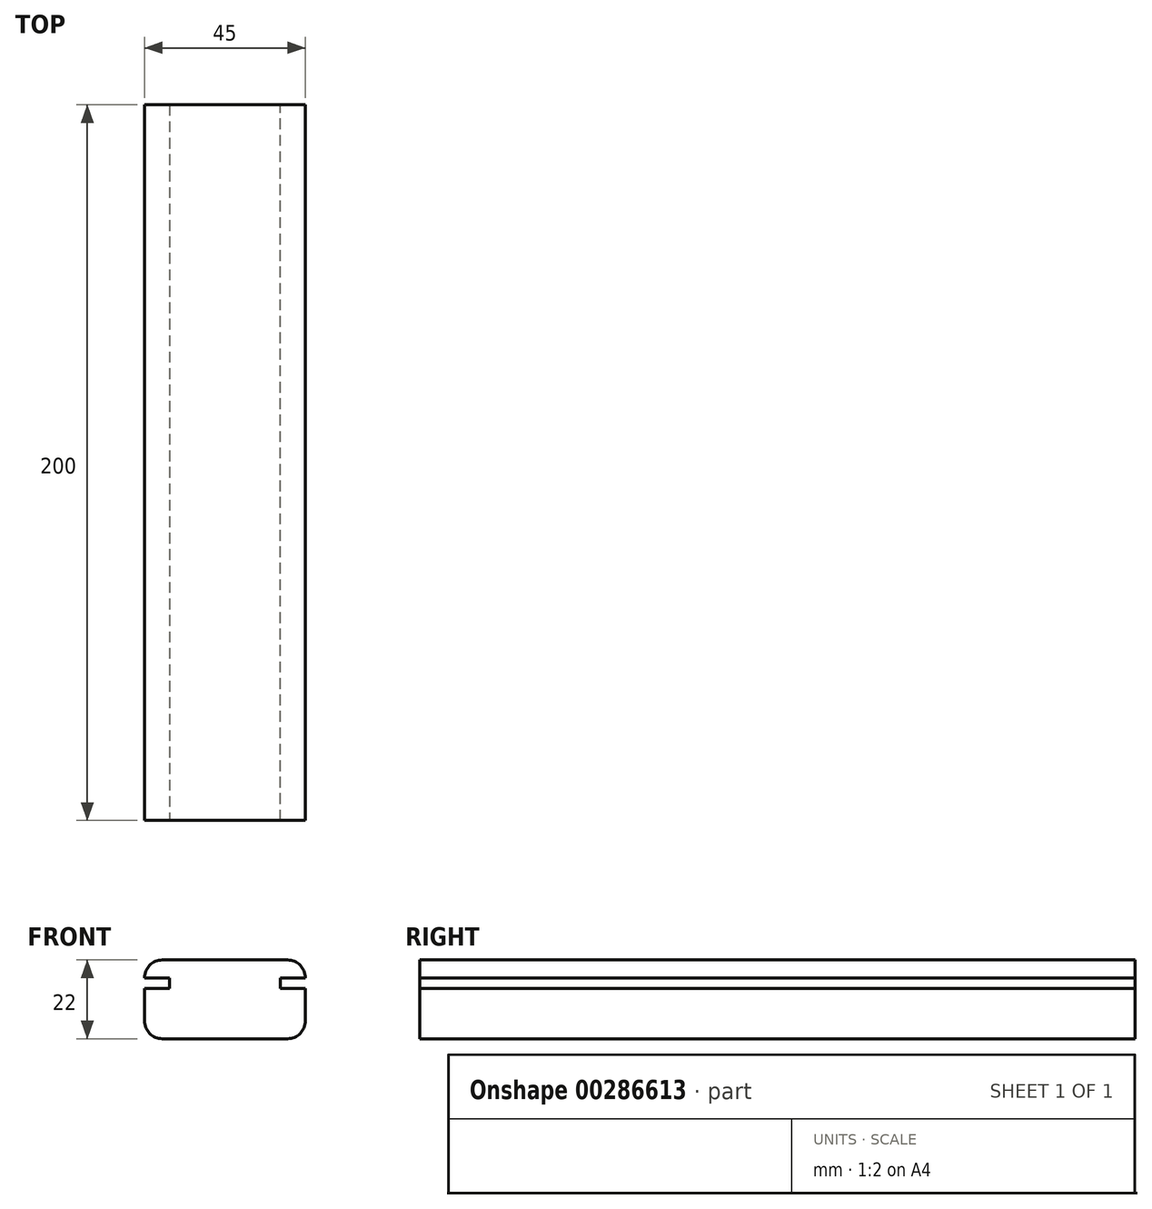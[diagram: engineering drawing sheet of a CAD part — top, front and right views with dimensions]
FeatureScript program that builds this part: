
annotation { "Feature Type Name" : "Feature", "Feature Type Description" : "" }
export const myFeature = defineFeature(function(context is Context, id is Id, definition is map)
    precondition{}
    {
        {
            var Q0;
            Q0=qCreatedBy(makeId("Front.planeOp"),FACE);
            var sketch = newSketch(context, id + "F0", { "sketchPlane" : qUnion([Q0])});
            skLineSegment(sketch, "E0.bottom", {"start": v(-22.5, 11) * mm, "end": v(22.5, 11) * mm});
            skLineSegment(sketch, "E0.top", {"start": v(-22.5, -11) * mm, "end": v(22.5, -11) * mm});
            skLineSegment(sketch, "E0.left", {"start": v(-22.5, 11) * mm, "end": v(-22.5, -11) * mm});
            skLineSegment(sketch, "E0.right", {"start": v(22.5, 11) * mm, "end": v(22.5, -11) * mm});
            skPoint(sketch, "E0.middle", {"position": v(0, 0) * mm});
            skSolve(sketch);
        }
        {
            var Q0;
            Q0=makeQuery(id+"F0.imprint","IMPRINT",FACE,{"disambiguationData":[TD([[makeQuery(id+"F0.imprint","IMPRINT",EDGE,{"derivedFrom":sQuery(id+"F0.wireOp",EDGE,"E0.bottom")}),-1.0]])]});
            extrude(context, id + "F1", {"entities" : qUnion([Q0]), "oppositeDirection" : true, "depth" : 200 * mm});
        }
        {
            var Q0;
            Q0=makeQuery(id+"F1.opExtrude","SWEPT_EDGE",EDGE,{"disambiguationData":[OSD([sQuery(id+"F0.wireOp",EDGE,"E0.bottom"),sQuery(id+"F0.wireOp",EDGE,"E0.right")])]});
            var Q1;
            Q1=makeQuery(id+"F1.opExtrude","SWEPT_EDGE",EDGE,{"disambiguationData":[OSD([sQuery(id+"F0.wireOp",EDGE,"E0.bottom"),sQuery(id+"F0.wireOp",EDGE,"E0.left")])]});
            var Q2;
            Q2=makeQuery(id+"F1.opExtrude","SWEPT_EDGE",EDGE,{"disambiguationData":[OSD([sQuery(id+"F0.wireOp",EDGE,"E0.top"),sQuery(id+"F0.wireOp",EDGE,"E0.right")])]});
            var Q3;
            Q3=makeQuery(id+"F1.opExtrude","SWEPT_EDGE",EDGE,{"disambiguationData":[OSD([sQuery(id+"F0.wireOp",EDGE,"E0.top"),sQuery(id+"F0.wireOp",EDGE,"E0.left")])]});
            fillet(context, id + "F2", {"entities" : qUnion([Q0, Q1, Q2, Q3]), "radius" : 5 * mm, "tangentPropagation" : true, "allowEdgeOverflow" : false});
        }
        {
            var Q0;
            Q0=makeQuery(id+"F1.opExtrude","SWEPT_FACE",FACE,{"disambiguationData":[OSD([sQuery(id+"F0.wireOp",EDGE,"E0.right")])]});
            var sketch = newSketch(context, id + "F3", { "sketchPlane" : qUnion([Q0])});
            skLineSegment(sketch, "E1.bottom", {"start": v(0, 3) * mm, "end": v(200, 3) * mm});
            skLineSegment(sketch, "E1.top", {"start": v(0, 6) * mm, "end": v(200, 6) * mm});
            skLineSegment(sketch, "E1.left", {"start": v(0, 3) * mm, "end": v(0, 6) * mm});
            skLineSegment(sketch, "E1.right", {"start": v(200, 3) * mm, "end": v(200, 6) * mm});
            skSolve(sketch);
        }
        {
            var Q0;
            {var subQ0=sQuery(id+"F3.wireOp",EDGE,"E1.top");Q0=makeQuery(id+"F3.imprint","IMPRINT",FACE,{"disambiguationData":[TD([[makeQuery(id+"F3.imprint","IMPRINT",EDGE,{"derivedFrom":subQ0}),-1.0]])]});}
            var Q1;
            {var subQ0=sQuery(id+"F3.wireOp",EDGE,"E1.bottom");Q1=makeQuery(id+"F3.imprint","IMPRINT",FACE,{"disambiguationData":[TD([[makeQuery(id+"F3.imprint","IMPRINT",EDGE,{"derivedFrom":subQ0}),1.0]])]});}
            extrude(context, id + "F4", {"entities" : qUnion([Q0, Q1]), "operationType" : NewBodyOperationType.REMOVE, "oppositeDirection" : true, "depth" : 7 * mm});
        }
        {
            var Q0;
            Q0=makeQuery(id+"F1.opExtrude","SWEPT_FACE",FACE,{"disambiguationData":[OSD([sQuery(id+"F0.wireOp",EDGE,"E0.left")])]});
            var sketch = newSketch(context, id + "F5", { "sketchPlane" : qUnion([Q0])});
            skLineSegment(sketch, "E2.bottom", {"start": v(-200, 3) * mm, "end": v(0, 3) * mm});
            skLineSegment(sketch, "E2.top", {"start": v(-200, 6) * mm, "end": v(0, 6) * mm});
            skLineSegment(sketch, "E2.left", {"start": v(-200, 3) * mm, "end": v(-200, 6) * mm});
            skLineSegment(sketch, "E2.right", {"start": v(0, 3) * mm, "end": v(0, 6) * mm});
            skSolve(sketch);
        }
        {
            var Q0;
            Q0=makeQuery(id+"F5.imprint","IMPRINT",FACE,{"disambiguationData":[TD([[makeQuery(id+"F5.imprint","IMPRINT",EDGE,{"derivedFrom":sQuery(id+"F5.wireOp",EDGE,"E2.bottom")}),1.0]])]});
            extrude(context, id + "F6", {"entities" : qUnion([Q0]), "operationType" : NewBodyOperationType.REMOVE, "oppositeDirection" : true, "depth" : 7 * mm});
        }
    });
